# Revit family: Faucet_Contemporary_Soiree_TB960S_TOTO
name_source: partatom
category: Plumbing Fixtures
revit_build: Autodesk Revit Architecture 2013 (Build: 20130531_2115(x64)
units: mm (PartAtom-declared; Revit-internal decimal feet)

## types (1)
- TB960S
    04 CSI = 22 41 39
    95 CSI = 15416
    ADA Compliant = Yes
    Apparent Power = 0 VA
    Assembly Code = D2010310
    CAD Drawing URL = http://assets.totousa.com
    CW Connection = Yes
    CWFU = 0
    Cold Water Connection NPT Radius = 1/4"
    Color Availability = #CP Polished Chrome
    Current = 0 A
    Default Elevation = 48"
    Depth = 9 7/8"
    Description = 5 Hole Deck Bath Trim
    Finish = Metal - TOTO - Chrome - Polished
    Flow Pressure = 0.00 psi
    Flow Rate = 0 GPM
    Frequency = 0 Hz
    HW Connection = Yes
    HWFU = 0
    Height = 7 3/4"
    Hot Water Connection NPT Radius = 1/4"
    Manufacturer = TOTO USA, Inc.
    Manufacturer Fax = (770) 282-0002
    Model = TB960S
    Number of Poles = 1
    Series = Soiree
    Shipping Weight = 13.20 lb
    Spec Sheet URL = http://assets.totousa.com
    Style = Contemporary
    Subcategory = Faucets
    Toto BIM Number = BM-00054
    URL = http://www.totousa.com
    Vent Connection = Yes
    Voltage = 0 V
    Warranty = Lifetime Limited Warranty (Residential Use); One Year Limited (Commercial Use)
    Warranty URL = http://www.totousa.com
    Waste Connection = No
    Width = 23 13/32"

## geometry (parser evidence)
native form markers: Blend x24, Sweep x5
no freeform markers — native parametric forms only
